# Revit family: PRD_FrankeWS_ClthsHks_FIRMUSRobeHook_FIRX010HP
name_source: partatom
category: Specialty Equipment
revit_build: Autodesk Revit 2018 (Build: 20190510_1515(x64)
units: mm (PartAtom-declared; Revit-internal decimal feet)

## family parameters
Cut with Voids When Loaded = No
Host = Face
OmniClass Number = 23.40.20.21.31
OmniClass Title = Robe Hooks
Part Type = Normal
Room Calculation Point = No
Round Connector Dimension = Use Diameter
Shared = No

## types (1)
- FIRX010HP
    AssetType = Fixed
    BIMObjectName = PRD_AR_ClothesHooks_FIRMUSRobeHook_FIRX010HP
    Category = Pr_40_30_78_15, Clothes hooks
    Default Elevation = 1600 mm  [stored 5.24934 ft]
    Description = Single robe hook for wall mounting, 304 stainless steel, round covers with drilled hole on bottom for fixation, inclusive stainless steel screws and dowels.
    DurationUnit = year
    Features = stainless steel, high polished
    Finish = high polished
    GrossWeight = 0.16 kg
    HookMaterial = PRD_AR_StainlessSteel_HighPolished
    IfcExportAs = IfcFurnitureType
    IfcExportType = USERDEFINED
    IntegralAccessories = incl. stainless steel screws and dowels
    IsBuiltIn = TRUE
    MainColor = stainless steel
    Manufacturer = KWC Group AG
    ManufacturerName = KWC Group AG
    ManufacturerURL = www.kwc.com
    Material = stainless steel
    MaterialCode = 1.4301
    Model = FIRX010HP
    ModelNumber = 2000106279
    ModelReference = FIRX010HP
    NBSDescription = Clothes hooks
    NBSReference = 45-35-72/322
    Name = Robe hook FIRX010HP
    NetWeight = 0.12 kg
    NominalDepth = 54 mm  [stored 0.177165 ft]
    NominalHeight = 60 mm  [stored 0.19685 ft]
    NominalWidth = 60 mm  [stored 0.19685 ft]
    NumberOfHooks = 1
    ProductInformation = https://pim.kwc.com
    Size = 60 x 60 x 54 mm
    Style = Hook
    TypeOfFixing = Screw
    TypeOfMounting = Wall mounting
    URL = www.kwc.com
    Uniclass2015Code = Pr_40_30_78_15
    Uniclass2015Title = Clothes hooks
    Uniclass2015Version = Products v1.17
    Version = 1
    WarrantyDurationUnit = year

note: [stored X ft] marks values corroborated as IEEE doubles in the binary element streams (Revit-internal decimal feet)

## geometry (parser evidence)
native form markers: Sweep x2
no freeform markers — native parametric forms only
